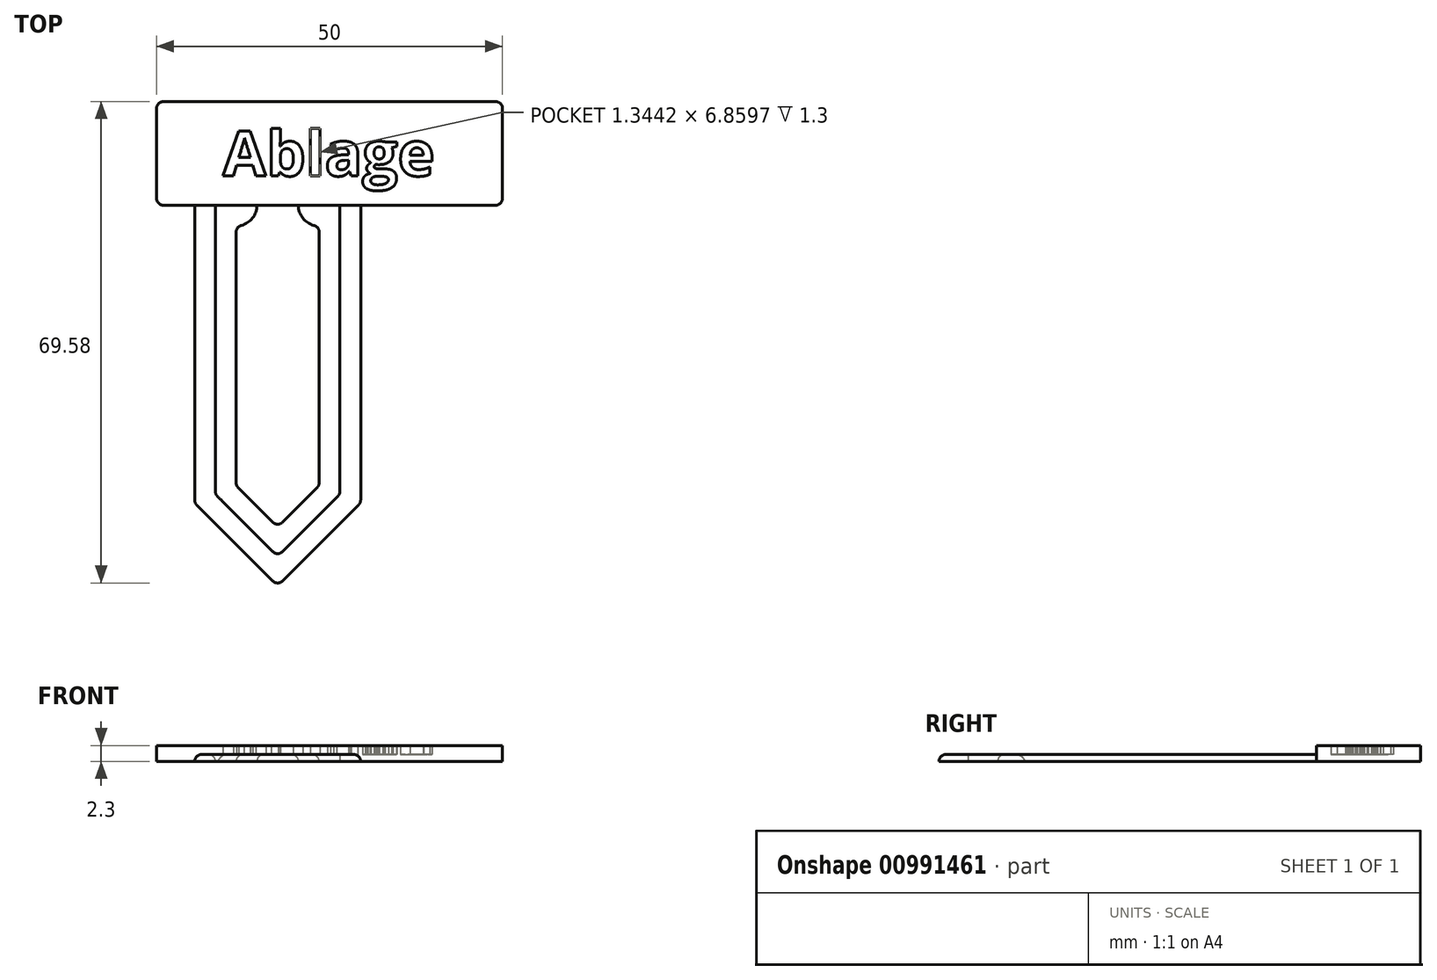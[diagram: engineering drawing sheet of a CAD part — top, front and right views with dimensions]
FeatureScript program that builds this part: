
annotation { "Feature Type Name" : "Feature", "Feature Type Description" : "" }
export const myFeature = defineFeature(function(context is Context, id is Id, definition is map)
    precondition{}
    {
        {
            var Q0;
            Q0=qCreatedBy(makeId("Top.planeOp"),FACE);
            var sketch = newSketch(context, id + "F0", { "sketchPlane" : qUnion([Q0])});
            skLineSegment(sketch, "E0", {"start": v(-14.18, 18.01) * mm, "end": v(-14.18, -24.99) * mm});
            skLineSegment(sketch, "E1", {"start": v(-11.18, 18.01) * mm, "end": v(-11.18, -23.75) * mm});
            skLineSegment(sketch, "E2", {"start": v(-8.18, 15.01) * mm, "end": v(-8.18, -22.5) * mm});
            skLineSegment(sketch, "E3", {"start": v(-2.18, 18.01) * mm, "end": v(-2.18, -9.23) * mm, "construction": true});
            skLineSegment(sketch, "E4", {"start": v(-8.18, -22.5) * mm, "end": v(-2.18, -28.5) * mm});
            skLineSegment(sketch, "E5", {"start": v(-11.18, -23.75) * mm, "end": v(-2.18, -32.75) * mm});
            skLineSegment(sketch, "E6", {"start": v(-2.18, -36.99) * mm, "end": v(-14.18, -24.99) * mm});
            skLineSegment(sketch, "E7.MirrorCS", {"start": v(9.82, 18.01) * mm, "end": v(9.82, -24.99) * mm});
            skLineSegment(sketch, "E8.MirrorCS", {"start": v(6.82, 18.01) * mm, "end": v(6.82, -23.75) * mm});
            skLineSegment(sketch, "E9.MirrorCS", {"start": v(3.82, -22.5) * mm, "end": v(-2.18, -28.5) * mm});
            skLineSegment(sketch, "E10.MirrorCS", {"start": v(6.82, -23.75) * mm, "end": v(-2.18, -32.75) * mm});
            skLineSegment(sketch, "E11.MirrorCS", {"start": v(3.82, 15.01) * mm, "end": v(3.82, -22.5) * mm});
            skLineSegment(sketch, "E12.MirrorCS", {"start": v(-2.18, -36.99) * mm, "end": v(9.82, -24.99) * mm});
            skLineSegment(sketch, "E13.bottom", {"start": v(30.32, 18.01) * mm, "end": v(-19.68, 18.01) * mm});
            skLineSegment(sketch, "E13.top", {"start": v(30.32, 33.01) * mm, "end": v(-19.68, 33.01) * mm});
            skLineSegment(sketch, "E13.left", {"start": v(30.32, 18.01) * mm, "end": v(30.32, 33.01) * mm});
            skLineSegment(sketch, "E13.right", {"start": v(-19.68, 18.01) * mm, "end": v(-19.68, 33.01) * mm});
            skArc(sketch, "E14", {"start": v(-5.18, 18.01) * mm, "mid": v(-6.06, 15.9) * mm, "end": v(-8.18, 15.01) * mm});
            skArc(sketch, "E15", {"start": v(0.82, 18.01) * mm, "mid": v(1.7, 15.9) * mm, "end": v(3.82, 15.01) * mm});
            skText(sketch, "E16", { "text": "Ablage", "fontName": "OpenSans-Bold.ttf"});
            skLineSegment(sketch, "E17", {"start": v(5.32, 33.01) * mm, "end": v(5.32, 18.01) * mm, "construction": true});
            skLineSegment(sketch, "E18", {"start": v(-19.68, 25.51) * mm, "end": v(30.32, 25.51) * mm, "construction": true});
            const initialGuessF0  = {"E16": [-0.01007, 0.02226, 1, 0, 0.0065]};
            skSetInitialGuess(sketch, initialGuessF0);
            skSolve(sketch);
        }
        {
            var Q0;
            {var subQ1=sQuery(id+"F0.wireOp",EDGE,"E0");Q0=makeQuery(id+"F0.imprint","IMPRINT",FACE,{"disambiguationData":[TD([[makeQuery(id+"F0.imprint","IMPRINT",EDGE,{"derivedFrom":subQ1}),1.0]])]});}
            var Q1;
            Q1=makeQuery(id+"F0.imprint","IMPRINT",FACE,{"disambiguationData":[TD([[makeQuery(id+"F0.imprint","IMPRINT",EDGE,{"derivedFrom":sQuery(id+"F0.wireOp",EDGE,"E2")}),1.0]])]});
            var Q2;
            Q2=makeQuery(id+"F0.imprint","IMPRINT",FACE,{"disambiguationData":[TD([[makeQuery(id+"F0.imprint","IMPRINT",EDGE,{"derivedFrom":sQuery(id+"F0.wireOp",EDGE,"E16.sketch_text.stroke-0")}),-1.0]])]});
            var Q3;
            Q3=makeQuery(id+"F0.imprint","IMPRINT",FACE,{"disambiguationData":[TD([[makeQuery(id+"F0.imprint","IMPRINT",EDGE,{"derivedFrom":sQuery(id+"F0.wireOp",EDGE,"E16.sketch_text.stroke-12")}),-1.0]])]});
            var Q4;
            Q4=makeQuery(id+"F0.imprint","IMPRINT",FACE,{"disambiguationData":[TD([[makeQuery(id+"F0.imprint","IMPRINT",EDGE,{"derivedFrom":sQuery(id+"F0.wireOp",EDGE,"E16.sketch_text.stroke-35")}),-1.0]])]});
            var Q5;
            Q5=makeQuery(id+"F0.imprint","IMPRINT",FACE,{"disambiguationData":[TD([[makeQuery(id+"F0.imprint","IMPRINT",EDGE,{"derivedFrom":sQuery(id+"F0.wireOp",EDGE,"E16.sketch_text.stroke-39")}),-1.0]])]});
            var Q6;
            Q6=makeQuery(id+"F0.imprint","IMPRINT",FACE,{"disambiguationData":[TD([[makeQuery(id+"F0.imprint","IMPRINT",EDGE,{"derivedFrom":sQuery(id+"F0.wireOp",EDGE,"E16.sketch_text.stroke-64")}),-1.0]])]});
            var Q7;
            Q7=makeQuery(id+"F0.imprint","IMPRINT",FACE,{"disambiguationData":[TD([[makeQuery(id+"F0.imprint","IMPRINT",EDGE,{"derivedFrom":sQuery(id+"F0.wireOp",EDGE,"E16.sketch_text.stroke-108")}),-1.0]])]});
            extrude(context, id + "F1", {"entities" : qUnion([Q0, Q1, Q2, Q3, Q4, Q5, Q6, Q7]), "depth" : 1 * mm, "offsetDistance" : 25 * mm});
        }
        {
            var Q0;
            Q0=makeQuery(id+"F0.imprint","IMPRINT",FACE,{"disambiguationData":[TD([[makeQuery(id+"F0.imprint","IMPRINT",EDGE,{"derivedFrom":sQuery(id+"F0.wireOp",EDGE,"E13.top")}),1.0]])]});
            var Q1;
            Q1=makeQuery(id+"F0.imprint","IMPRINT",FACE,{"disambiguationData":[TD([[makeQuery(id+"F0.imprint","IMPRINT",EDGE,{"derivedFrom":sQuery(id+"F0.wireOp",EDGE,"E16.sketch_text.stroke-8")}),1.0]])]});
            var Q2;
            Q2=makeQuery(id+"F0.imprint","IMPRINT",FACE,{"disambiguationData":[TD([[makeQuery(id+"F0.imprint","IMPRINT",EDGE,{"derivedFrom":sQuery(id+"F0.wireOp",EDGE,"E16.sketch_text.stroke-26")}),1.0]])]});
            var Q3;
            Q3=makeQuery(id+"F0.imprint","IMPRINT",FACE,{"disambiguationData":[TD([[makeQuery(id+"F0.imprint","IMPRINT",EDGE,{"derivedFrom":sQuery(id+"F0.wireOp",EDGE,"E16.sketch_text.stroke-57")}),1.0]])]});
            var Q4;
            Q4=makeQuery(id+"F0.imprint","IMPRINT",FACE,{"disambiguationData":[TD([[makeQuery(id+"F0.imprint","IMPRINT",EDGE,{"derivedFrom":sQuery(id+"F0.wireOp",EDGE,"E16.sketch_text.stroke-102")}),1.0]])]});
            var Q5;
            Q5=makeQuery(id+"F0.imprint","IMPRINT",FACE,{"disambiguationData":[TD([[makeQuery(id+"F0.imprint","IMPRINT",EDGE,{"derivedFrom":sQuery(id+"F0.wireOp",EDGE,"E16.sketch_text.stroke-93")}),1.0]])]});
            var Q6;
            Q6=makeQuery(id+"F0.imprint","IMPRINT",FACE,{"disambiguationData":[TD([[makeQuery(id+"F0.imprint","IMPRINT",EDGE,{"derivedFrom":sQuery(id+"F0.wireOp",EDGE,"E16.sketch_text.stroke-108")}),1.0]])]});
            extrude(context, id + "F2", {"entities" : qUnion([Q0, Q1, Q2, Q3, Q4, Q5, Q6]), "operationType" : NewBodyOperationType.ADD, "depth" : 2.3 * mm, "offsetDistance" : 25 * mm});
        }
        {
            var Q0;
            Q0=makeQuery(id+"F2.opExtrude","SWEPT_EDGE",EDGE,{"disambiguationData":[OSD([sQuery(id+"F0.wireOp",EDGE,"E13.top"),sQuery(id+"F0.wireOp",EDGE,"E13.right")])]});
            var Q1;
            Q1=makeQuery(id+"F2.opExtrude","SWEPT_EDGE",EDGE,{"disambiguationData":[OSD([sQuery(id+"F0.wireOp",EDGE,"E13.bottom"),sQuery(id+"F0.wireOp",EDGE,"E13.right")])]});
            var Q2;
            Q2=makeQuery(id+"F1.opExtrude","SWEPT_EDGE",EDGE,{"disambiguationData":[OSD([sQuery(id+"F0.wireOp",EDGE,"E2"),sQuery(id+"F0.wireOp",EDGE,"E14")])]});
            var Q3;
            Q3=makeQuery(id+"F1.opExtrude","SWEPT_EDGE",EDGE,{"disambiguationData":[OSD([sQuery(id+"F0.wireOp",EDGE,"E2"),sQuery(id+"F0.wireOp",EDGE,"E4")])]});
            var Q4;
            Q4=makeQuery(id+"F1.opExtrude","SWEPT_EDGE",EDGE,{"disambiguationData":[OSD([sQuery(id+"F0.wireOp",EDGE,"E0"),sQuery(id+"F0.wireOp",EDGE,"E6")])]});
            var Q5;
            Q5=makeQuery(id+"F1.opExtrude","SWEPT_EDGE",EDGE,{"disambiguationData":[OSD([sQuery(id+"F0.wireOp",EDGE,"E4"),sQuery(id+"F0.wireOp",EDGE,"E9.MirrorCS")])]});
            var Q6;
            Q6=makeQuery(id+"F1.opExtrude","SWEPT_EDGE",EDGE,{"disambiguationData":[OSD([sQuery(id+"F0.wireOp",EDGE,"E6"),sQuery(id+"F0.wireOp",EDGE,"E12.MirrorCS")])]});
            var Q7;
            Q7=makeQuery(id+"F1.opExtrude","SWEPT_EDGE",EDGE,{"disambiguationData":[OSD([sQuery(id+"F0.wireOp",EDGE,"E8.MirrorCS"),sQuery(id+"F0.wireOp",EDGE,"E10.MirrorCS")])]});
            var Q8;
            Q8=makeQuery(id+"F1.opExtrude","SWEPT_EDGE",EDGE,{"disambiguationData":[OSD([sQuery(id+"F0.wireOp",EDGE,"E11.MirrorCS"),sQuery(id+"F0.wireOp",EDGE,"E15")])]});
            var Q9;
            Q9=makeQuery(id+"F2.opExtrude","SWEPT_EDGE",EDGE,{"disambiguationData":[OSD([sQuery(id+"F0.wireOp",EDGE,"E13.bottom"),sQuery(id+"F0.wireOp",EDGE,"E13.left")])]});
            var Q10;
            Q10=makeQuery(id+"F2.opExtrude","SWEPT_EDGE",EDGE,{"disambiguationData":[OSD([sQuery(id+"F0.wireOp",EDGE,"E13.top"),sQuery(id+"F0.wireOp",EDGE,"E13.left")])]});
            var Q11;
            Q11=makeQuery(id+"F1.opExtrude","SWEPT_EDGE",EDGE,{"disambiguationData":[OSD([sQuery(id+"F0.wireOp",EDGE,"E7.MirrorCS"),sQuery(id+"F0.wireOp",EDGE,"E12.MirrorCS")])]});
            var Q12;
            Q12=makeQuery(id+"F1.opExtrude","SWEPT_EDGE",EDGE,{"disambiguationData":[OSD([sQuery(id+"F0.wireOp",EDGE,"E9.MirrorCS"),sQuery(id+"F0.wireOp",EDGE,"E11.MirrorCS")])]});
            var Q13;
            Q13=makeQuery(id+"F1.opExtrude","SWEPT_EDGE",EDGE,{"disambiguationData":[OSD([sQuery(id+"F0.wireOp",EDGE,"E1"),sQuery(id+"F0.wireOp",EDGE,"E5")])]});
            var Q14;
            Q14=makeQuery(id+"F1.opExtrude","SWEPT_EDGE",EDGE,{"disambiguationData":[OSD([sQuery(id+"F0.wireOp",EDGE,"E5"),sQuery(id+"F0.wireOp",EDGE,"E10.MirrorCS")])]});
            var Q15;
            Q15=makeQuery(id+"F1.opExtrude","CAP_EDGE",EDGE,{"disambiguationData":[OSD([sQuery(id+"F0.wireOp",EDGE,"E12.MirrorCS")])],"isStart":false});
            var Q16;
            Q16=makeQuery(id+"F1.opExtrude","CAP_EDGE",EDGE,{"disambiguationData":[OSD([sQuery(id+"F0.wireOp",EDGE,"E7.MirrorCS")])],"isStart":false});
            var Q17;
            Q17=makeQuery(id+"F1.opExtrude","CAP_EDGE",EDGE,{"disambiguationData":[OSD([sQuery(id+"F0.wireOp",EDGE,"E6")])],"isStart":false});
            var Q18;
            Q18=makeQuery(id+"F1.opExtrude","CAP_EDGE",EDGE,{"disambiguationData":[OSD([sQuery(id+"F0.wireOp",EDGE,"E0")])],"isStart":false});
            var Q19;
            Q19=makeQuery(id+"F1.opExtrude","CAP_EDGE",EDGE,{"disambiguationData":[OSD([sQuery(id+"F0.wireOp",EDGE,"E4")])],"isStart":false});
            var Q20;
            Q20=makeQuery(id+"F1.opExtrude","CAP_EDGE",EDGE,{"disambiguationData":[OSD([sQuery(id+"F0.wireOp",EDGE,"E9.MirrorCS")])],"isStart":false});
            var Q21;
            Q21=makeQuery(id+"F1.opExtrude","CAP_EDGE",EDGE,{"disambiguationData":[OSD([sQuery(id+"F0.wireOp",EDGE,"E11.MirrorCS")])],"isStart":false});
            var Q22;
            Q22=makeQuery(id+"F1.opExtrude","CAP_EDGE",EDGE,{"disambiguationData":[OSD([sQuery(id+"F0.wireOp",EDGE,"E2")])],"isStart":false});
            var Q23;
            Q23=makeQuery(id+"F1.opExtrude","CAP_EDGE",EDGE,{"disambiguationData":[OSD([sQuery(id+"F0.wireOp",EDGE,"E1")])],"isStart":false});
            var Q24;
            Q24=makeQuery(id+"F1.opExtrude","CAP_EDGE",EDGE,{"disambiguationData":[OSD([sQuery(id+"F0.wireOp",EDGE,"E15")])],"isStart":false});
            var Q25;
            Q25=makeQuery(id+"F1.opExtrude","CAP_EDGE",EDGE,{"disambiguationData":[OSD([sQuery(id+"F0.wireOp",EDGE,"E14")])],"isStart":false});
            fillet(context, id + "F3", {"entities" : qUnion([Q0, Q1, Q2, Q3, Q4, Q5, Q6, Q7, Q8, Q9, Q10, Q11, Q12, Q13, Q14, Q15, Q16, Q17, Q18, Q19, Q20, Q21, Q22, Q23, Q24, Q25]), "radius" : 1 * mm, "tangentPropagation" : true, "allowEdgeOverflow" : false});
        }
    });
